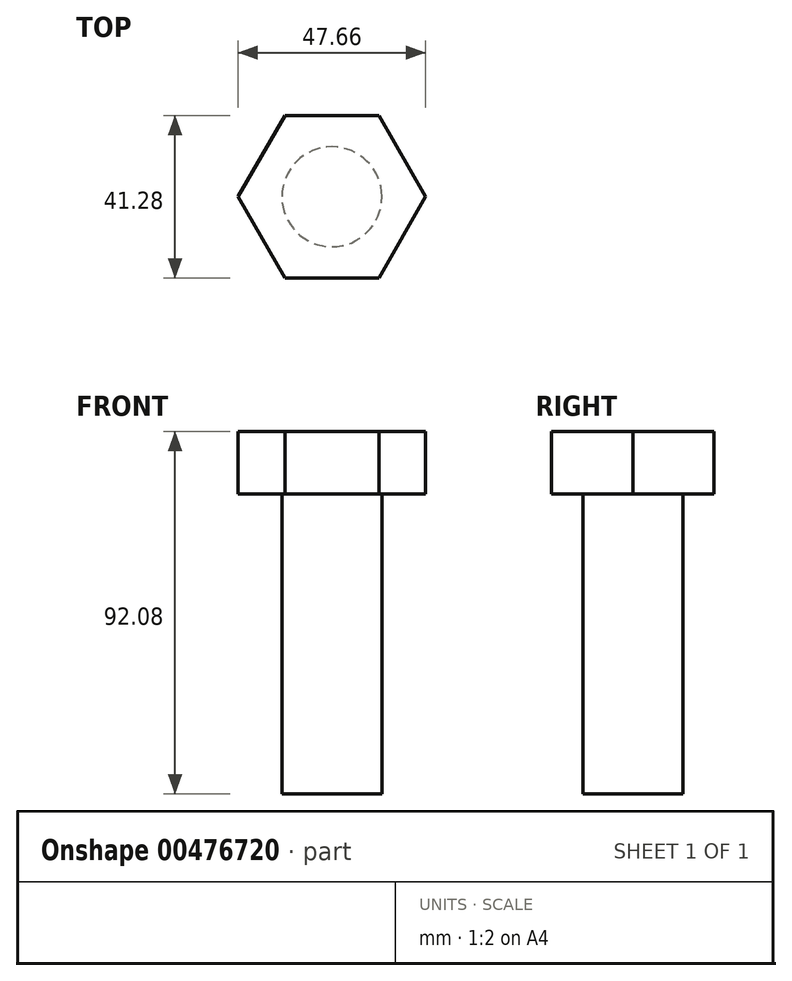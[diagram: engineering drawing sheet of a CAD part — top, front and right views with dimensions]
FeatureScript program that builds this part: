
annotation { "Feature Type Name" : "Feature", "Feature Type Description" : "" }
export const myFeature = defineFeature(function(context is Context, id is Id, definition is map)
    precondition{}
    {
        {
            var Q0;
            Q0=qCreatedBy(makeId("Top.planeOp"),FACE);
            var sketch = newSketch(context, id + "F0", { "sketchPlane" : qUnion([Q0])});
            skCircle(sketch, "E0", {"center": v(0, 0) * mm, "radius": 12.7 * mm});
            skSolve(sketch);
        }
        {
            var Q0;
            Q0=makeQuery(id+"F0.imprint","IMPRINT",FACE,{"disambiguationData":[TD([[makeQuery(id+"F0.imprint","IMPRINT",EDGE,{"derivedFrom":sQuery(id+"F0.wireOp",EDGE,"E0")}),1.0]])]});
            var Q1;
            Q1=qSketchRegion(id+"F2",true);
            extrude(context, id + "F1", {"entities" : qUnion([Q0, Q1]), "oppositeDirection" : true, "depth" : 38.1 * mm, "hasSecondDirection" : true, "secondDirectionOppositeDirection" : false, "secondDirectionDepth" : 38.1 * mm});
        }
        {
            var Q0;
            Q0=makeQuery(id+"F1.opExtrude","CAP_FACE",FACE,{"disambiguationData":[OSD([sQuery(id+"F0.wireOp",EDGE,"E0")])],"isStart":true});
            var sketch = newSketch(context, id + "F2", { "sketchPlane" : qUnion([Q0])});
            skCircle(sketch, "E1.cCircle", {"center": v(0, 0) * mm, "radius": 20.64 * mm, "construction": true});
            skLineSegment(sketch, "E1.0", {"start": v(-11.92, 20.64) * mm, "end": v(11.92, 20.64) * mm});
            skLineSegment(sketch, "E1.1", {"start": v(11.92, 20.64) * mm, "end": v(23.83, 0) * mm});
            skLineSegment(sketch, "E1.2", {"start": v(23.83, 0) * mm, "end": v(11.92, -20.64) * mm});
            skLineSegment(sketch, "E1.3", {"start": v(11.92, -20.64) * mm, "end": v(-11.92, -20.64) * mm});
            skLineSegment(sketch, "E1.4", {"start": v(-11.92, -20.64) * mm, "end": v(-23.83, 0) * mm});
            skLineSegment(sketch, "E1.5", {"start": v(-23.83, 0) * mm, "end": v(-11.92, 20.64) * mm});
            skPoint(sketch, "E1.0.midPoint", {"position": v(0, 20.64) * mm});
            skSolve(sketch);
        }
        {
            var Q0;
            Q0=qSketchRegion(id+"F2",true);
            extrude(context, id + "F3", {"entities" : qUnion([Q0]), "operationType" : NewBodyOperationType.ADD, "depth" : 15.88 * mm});
        }
    });
